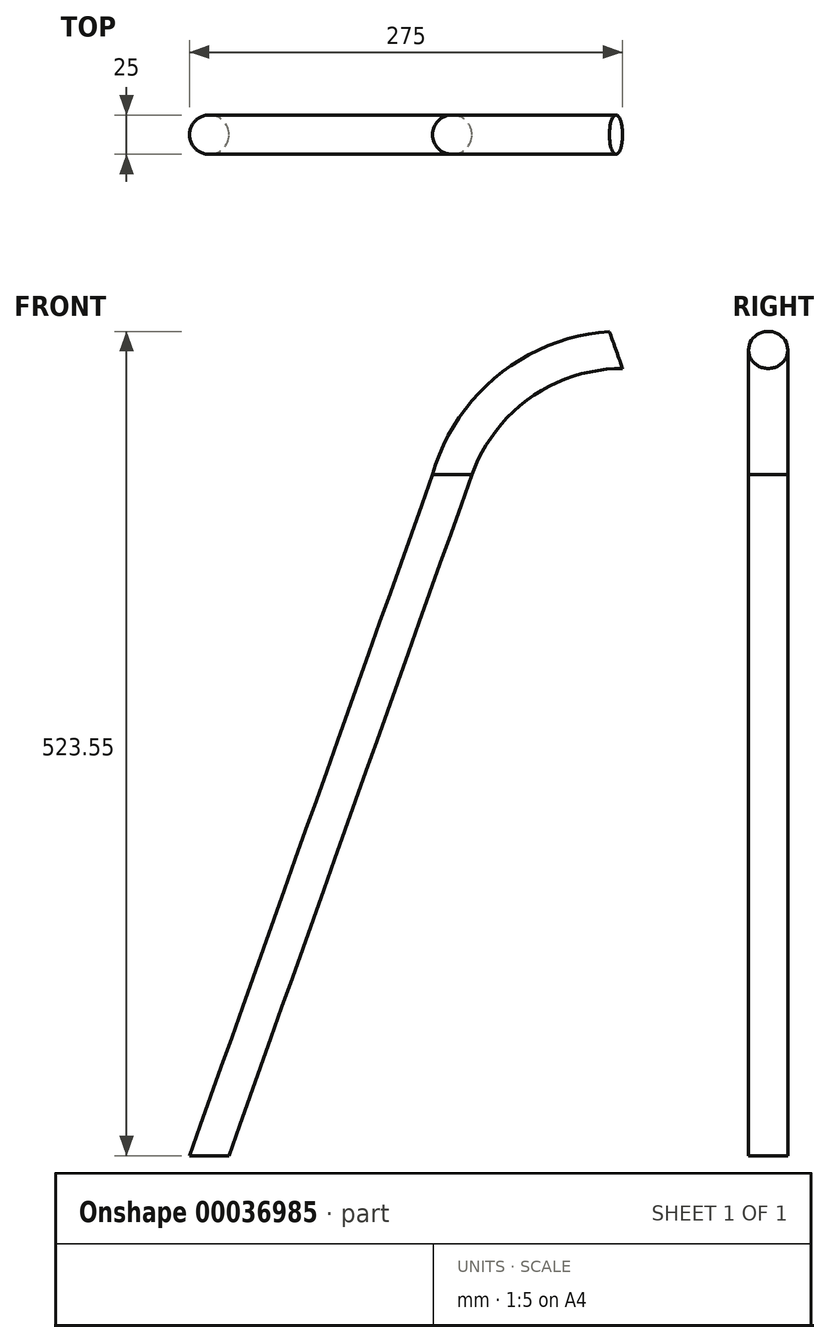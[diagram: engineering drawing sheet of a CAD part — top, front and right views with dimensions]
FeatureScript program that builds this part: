
annotation { "Feature Type Name" : "Feature", "Feature Type Description" : "" }
export const myFeature = defineFeature(function(context is Context, id is Id, definition is map)
    precondition{}
    {
        {
            var Q0;
            Q0=qCreatedBy(makeId("Top.planeOp"),FACE);
            var sketch = newSketch(context, id + "F0", { "sketchPlane" : qUnion([Q0])});
            skCircle(sketch, "E0", {"center": v(-12.5, 0) * mm, "radius": 12.5 * mm});
            skLineSegment(sketch, "E1", {"start": v(0, 0) * mm, "end": v(-12.5, 0) * mm, "construction": true});
            skSolve(sketch);
        }
        {
            var Q0;
            Q0=qCreatedBy(makeId("Front.planeOp"),FACE);
            var sketch = newSketch(context, id + "F1", { "sketchPlane" : qUnion([Q0])});
            skLineSegment(sketch, "E2", {"start": v(0, 0) * mm, "end": v(154.3, 432.54) * mm});
            skPoint(sketch, "E3.visualSharp", {"position": v(250, 700.78) * mm});
            skLineSegment(sketch, "E4", {"start": v(0, 0) * mm, "end": v(500, 0) * mm, "construction": true});
            skLineSegment(sketch, "E5", {"start": v(250, 700.78) * mm, "end": v(250, 0) * mm, "construction": true});
            skArc(sketch, "E6", {"start": v(250, 500) * mm, "mid": v(191.46, 481.44) * mm, "end": v(154.3, 432.54) * mm});
            skSolve(sketch);
        }
        {
            var Q0;
            Q0 = qSketchRegion(id + "F0", true);
            var Q1;
            Q1 = qConstructionFilter(qBodyType(qCreatedBy(id + "F1" ,EDGE), BodyType.WIRE), ConstructionObject.NO);
            sweep(context, id + "F2", {"profiles" : qUnion([Q0]), "path" : qUnion([Q1])});
        }
    });
